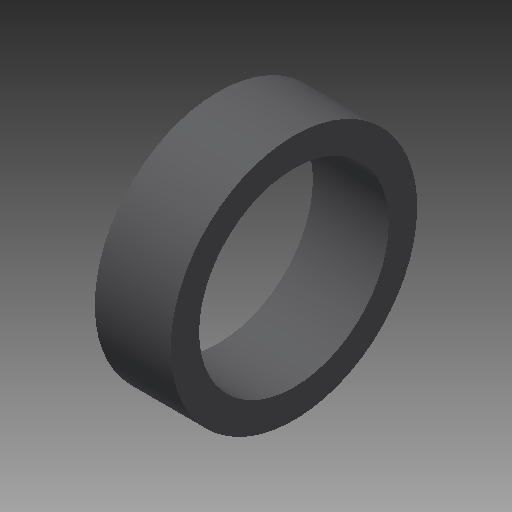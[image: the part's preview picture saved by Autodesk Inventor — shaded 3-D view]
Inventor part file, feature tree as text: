
AUTODESK INVENTOR PART (.ipt)
format: ipt  version: 2018 (Build 220112000, 112)  size: 104,448 bytes
history: native  units: mm
features: other x7, revolve x1, sketch x1
ambient origin geometry x8: Origin, YZ Plane, XZ Plane, XY Plane, X Axis, Y Axis, Z Axis, Center Point
bodies: Solid1 (feature_tree)
feature tree (9):
  revolve  "Revolution1"  [1 undecoded]
  other  "collar_XY"
  other  "collar_YZ"
  other  "collar_ZX"
  other  "collar_X"
  other  "collar_Y"
  other  "collar_Z"
  other  "collar_Center"
  sketch  "Sketch_1"  dims[d0=360.0deg d1=0.0mm]
note: 1 required parameter value undecoded (feature->parameter linkage not recoverable at this tier; creation-order binding heuristic only, values carry confidence <= 0.55)
